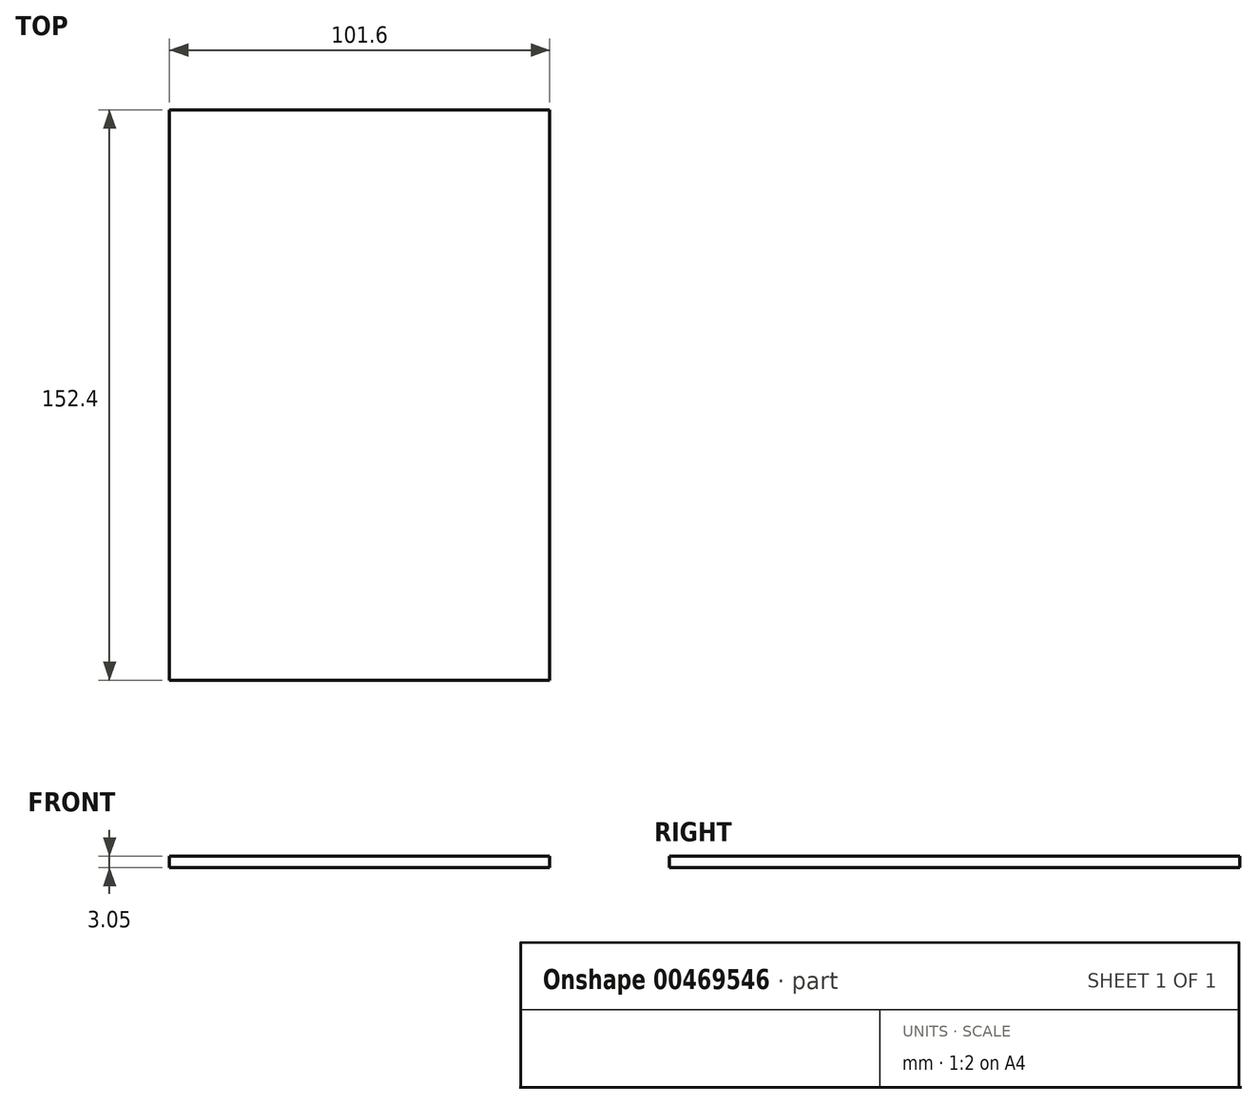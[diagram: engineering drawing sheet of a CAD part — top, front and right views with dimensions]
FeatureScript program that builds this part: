
annotation { "Feature Type Name" : "Feature", "Feature Type Description" : "" }
export const myFeature = defineFeature(function(context is Context, id is Id, definition is map)
    precondition{}
    {
        {
            var Q0;
            Q0=qCreatedBy(makeId("Top.planeOp"),FACE);
            var sketch = newSketch(context, id + "F0", { "sketchPlane" : qUnion([Q0])});
            skLineSegment(sketch, "E0.bottom", {"start": v(-50.8, -76.2) * mm, "end": v(50.8, -76.2) * mm});
            skLineSegment(sketch, "E0.top", {"start": v(-50.8, 76.2) * mm, "end": v(50.8, 76.2) * mm});
            skLineSegment(sketch, "E0.left", {"start": v(-50.8, -76.2) * mm, "end": v(-50.8, 76.2) * mm});
            skLineSegment(sketch, "E0.right", {"start": v(50.8, -76.2) * mm, "end": v(50.8, 76.2) * mm});
            skPoint(sketch, "E0.middle", {"position": v(0, 0) * mm});
            skSolve(sketch);
        }
        {
            var Q0;
            Q0 = qSketchRegion(id + "F0", true);
            extrude(context, id + "F1", {"entities" : qUnion([Q0]), "depth" : 3.05 * mm, "offsetDistance" : 25.4 * mm});
        }
    });
